FCSTD DOCUMENT  (FreeCAD 0.19R)
Label: screw_shc_M3x16
License: All rights reserved
LicenseURL: http://en.wikipedia.org/wiki/All_rights_reserved
objects: Part::Feature×1, PartDesign::ShapeBinder×1, PartDesign::CoordinateSystem×1, PartDesign::FeatureBase×1, PartDesign::Body×1
note: 5 computed .brp shape members not serialized (recipe doc carries the construction recipe); baked Part::Feature solids carry a one-line shape summary decoded from their .brp

FEATURE [Part::Feature] _1292A115_18_8_Stainless_Steel_Socket_Head_Screw
  shape: bbox 5.5 x 5.5 x 19.03 mm, 157 faces, 0 solids (baked)
FEATURE [PartDesign::ShapeBinder] Copy_1292A115_18_8_Stainless_Steel_Socket_Head_Screw
  TraceSupport = false
FEATURE [PartDesign::CoordinateSystem] Local_CS
  AttacherType = Attacher::AttachEngine3D
  MapMode = 11
  Placement = pos=(0,0,-16) rot=(-0.707107,0.707107,0;3.14159rad)
  Support = -> [Copy_1292A115_18_8_Stainless_Steel_Socket_Head_Screw]
FEATURE [PartDesign::FeatureBase] BaseFeature
  BaseFeature = -> _1292A115_18_8_Stainless_Steel_Socket_Head_Screw
FEATURE [PartDesign::Body] Body
  BaseFeature = -> _1292A115_18_8_Stainless_Steel_Socket_Head_Screw
  Group = -> [BaseFeature,Local_CS,Copy_1292A115_18_8_Stainless_Steel_Socket_Head_Screw]
  Origin = -> Origin
  Tip = -> BaseFeature
